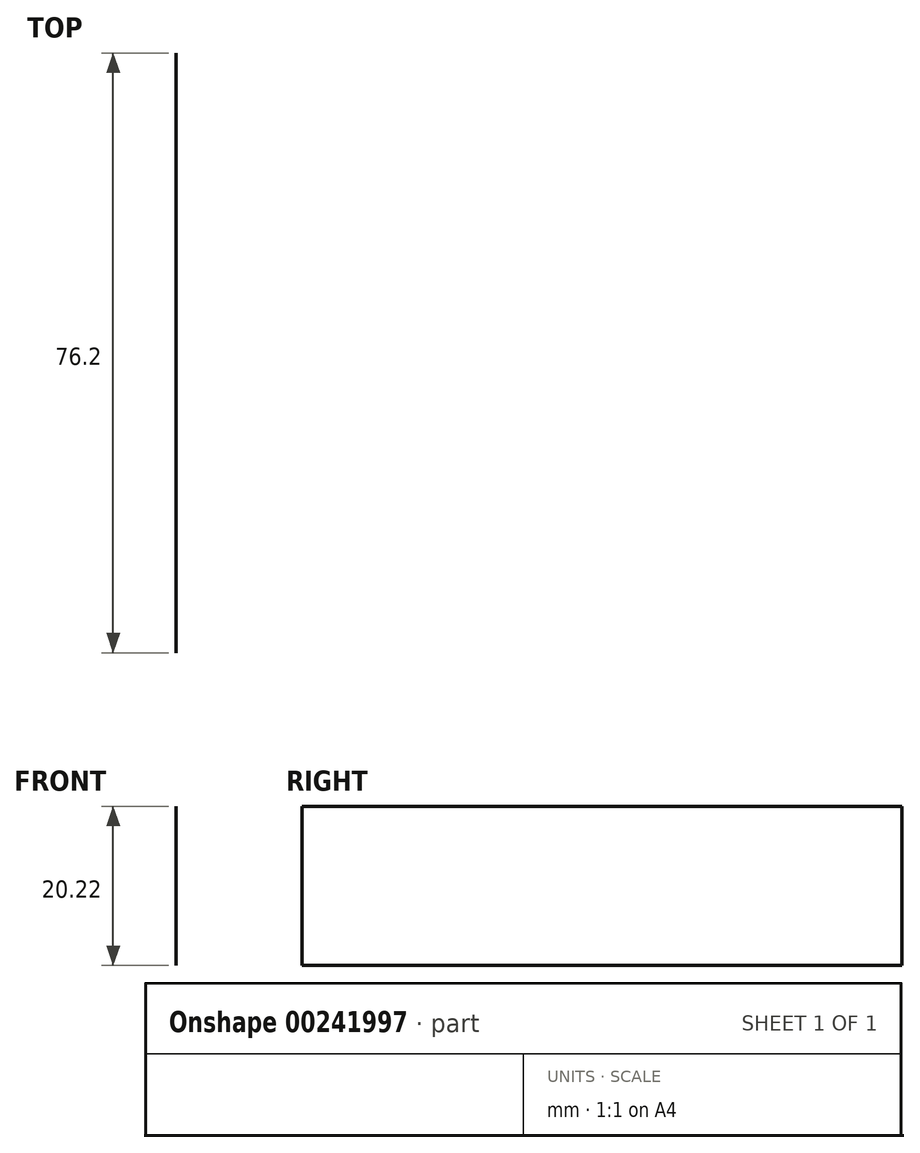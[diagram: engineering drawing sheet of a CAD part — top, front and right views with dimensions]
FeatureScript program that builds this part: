
annotation { "Feature Type Name" : "Feature", "Feature Type Description" : "" }
export const myFeature = defineFeature(function(context is Context, id is Id, definition is map)
    precondition{}
    {
        {
            var Q0;
            Q0=qCreatedBy(makeId("Front.planeOp"),FACE);
            var sketch = newSketch(context, id + "F0", { "sketchPlane" : qUnion([Q0])});
            skLineSegment(sketch, "E0.bottom", {"start": v(867.56, -260.7) * mm, "end": v(940, -260.7) * mm});
            skLineSegment(sketch, "E0.top", {"start": v(867.56, -280.92) * mm, "end": v(940, -280.92) * mm});
            skLineSegment(sketch, "E0.left", {"start": v(867.56, -260.7) * mm, "end": v(867.56, -280.92) * mm});
            skLineSegment(sketch, "E0.right", {"start": v(940, -260.7) * mm, "end": v(940, -280.92) * mm});
            skSolve(sketch);
        }
        {
            var Q0;
            Q0=sQuery(id+"F0.wireOp",EDGE,"E0.right");
            extrude(context, id + "F1", {"bodyType" : ToolBodyType.SURFACE, "surfaceEntities" : qUnion([Q0]), "depth" : 76.2 * mm});
        }
    });
